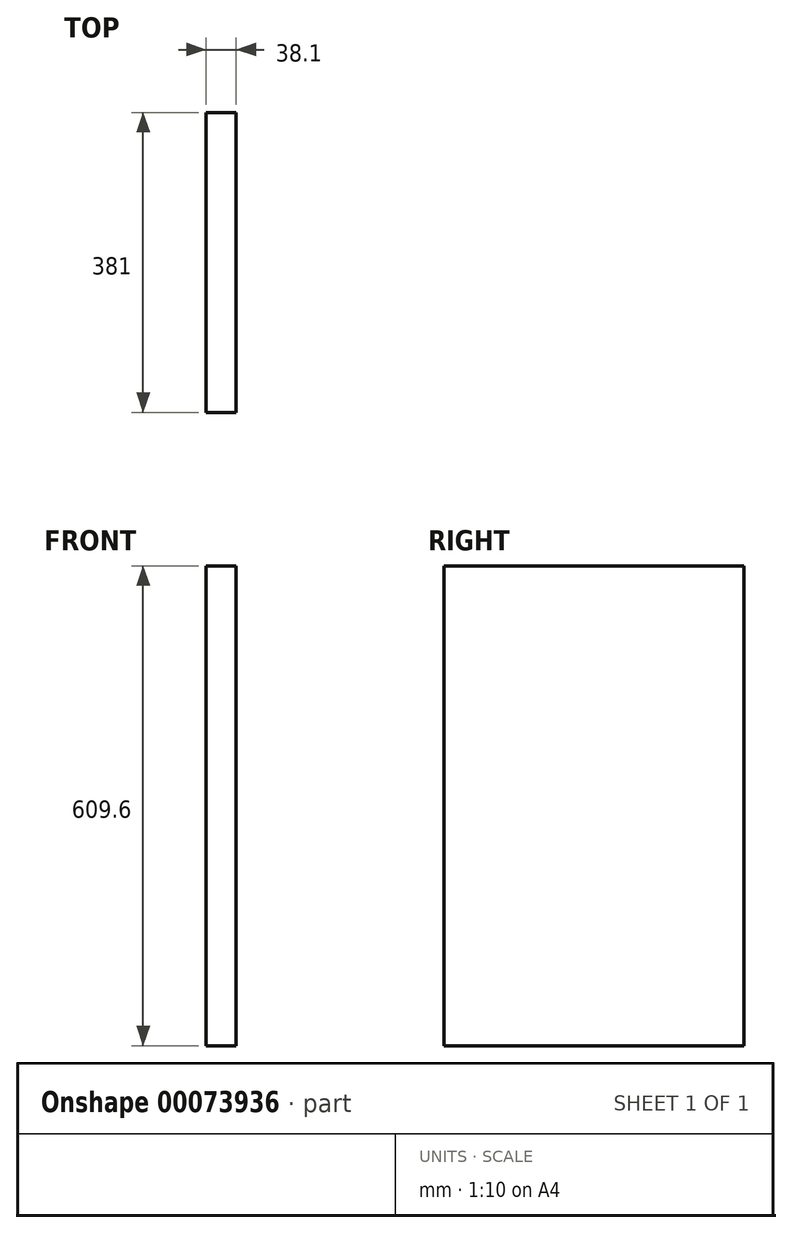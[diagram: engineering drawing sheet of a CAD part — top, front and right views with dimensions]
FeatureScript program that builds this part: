
annotation { "Feature Type Name" : "Feature", "Feature Type Description" : "" }
export const myFeature = defineFeature(function(context is Context, id is Id, definition is map)
    precondition{}
    {
        {
            var Q0;
            Q0=qCreatedBy(makeId("Front.planeOp"),FACE);
            var sketch = newSketch(context, id + "F0", { "sketchPlane" : qUnion([Q0])});
            skLineSegment(sketch, "E0.rect.bottom", {"start": v(-19.05, 304.8) * mm, "end": v(19.05, 304.8) * mm});
            skLineSegment(sketch, "E0.rect.top", {"start": v(-19.05, -304.8) * mm, "end": v(19.05, -304.8) * mm});
            skLineSegment(sketch, "E0.rect.left", {"start": v(-19.05, 304.8) * mm, "end": v(-19.05, -304.8) * mm});
            skLineSegment(sketch, "E0.rect.right", {"start": v(19.05, 304.8) * mm, "end": v(19.05, -304.8) * mm});
            skPoint(sketch, "E0.rect.middle", {"position": v(0, 0) * mm});
            skSolve(sketch);
        }
        {
            var Q0;
            Q0 = qSketchRegion(id + "F0", true);
            extrude(context, id + "F1", {"entities" : qUnion([Q0]), "oppositeDirection" : true, "depth" : 381 * mm});
        }
    });
